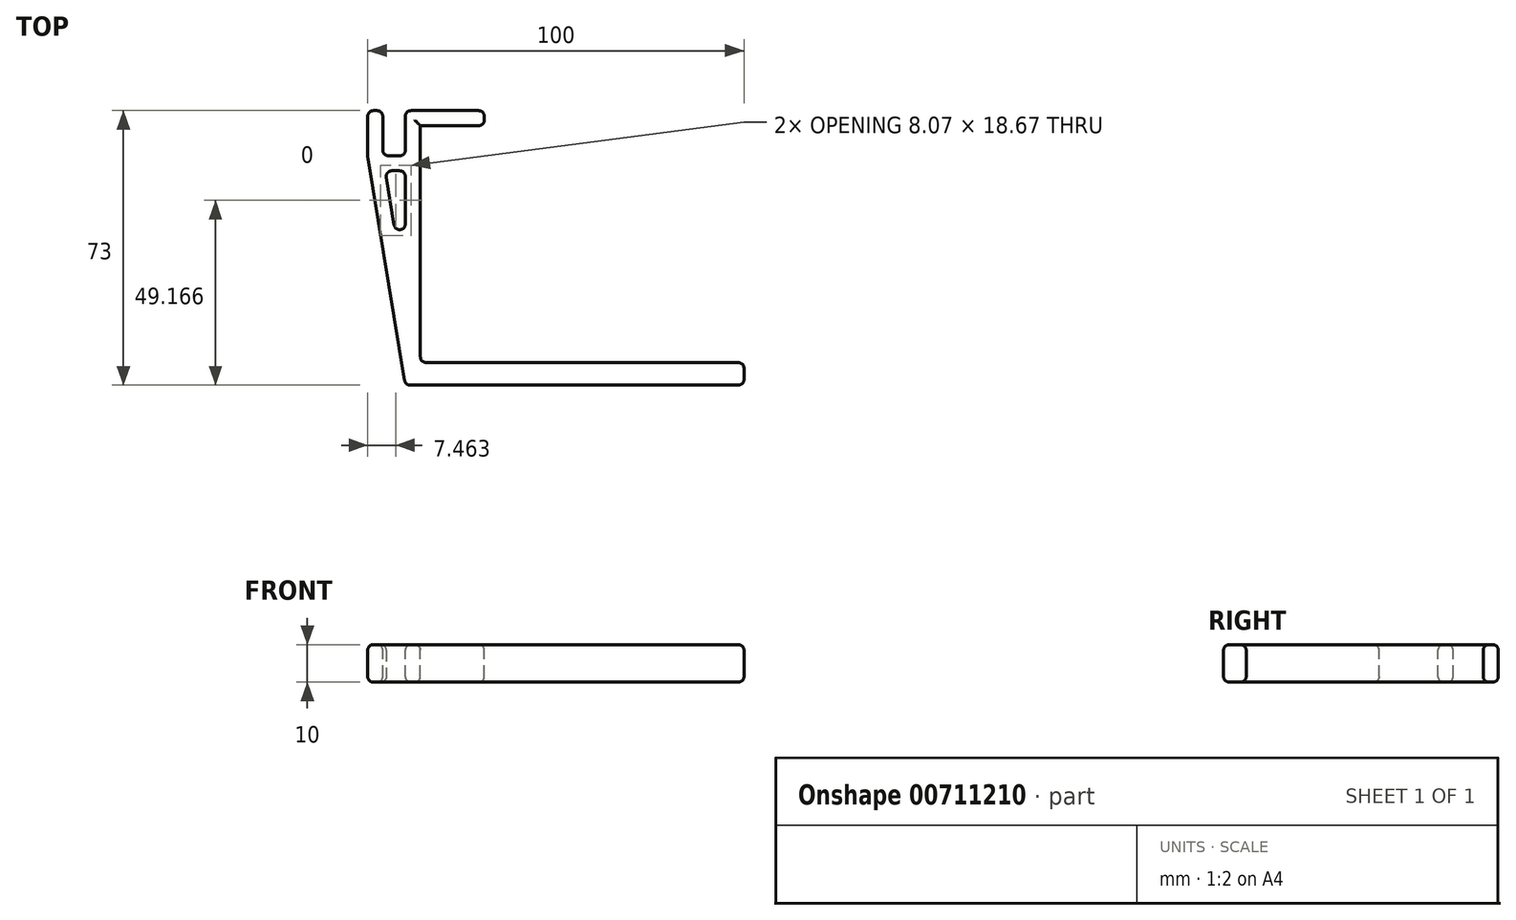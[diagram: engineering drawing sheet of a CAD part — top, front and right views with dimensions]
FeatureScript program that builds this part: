
annotation { "Feature Type Name" : "Feature", "Feature Type Description" : "" }
export const myFeature = defineFeature(function(context is Context, id is Id, definition is map)
    precondition{}
    {
        {
            var Q0;
            Q0=qCreatedBy(makeId("Top.planeOp"),FACE);
            var sketch = newSketch(context, id + "F0", { "sketchPlane" : qUnion([Q0])});
            skLineSegment(sketch, "E0", {"start": v(0, 0) * mm, "end": v(90, 0) * mm});
            skLineSegment(sketch, "E1", {"start": v(90, 6) * mm, "end": v(4, 6) * mm});
            skLineSegment(sketch, "E2", {"start": v(4, 6) * mm, "end": v(4, 69) * mm});
            skLineSegment(sketch, "E3", {"start": v(4, 69) * mm, "end": v(21, 69) * mm});
            skLineSegment(sketch, "E4", {"start": v(21, 69) * mm, "end": v(21, 73) * mm});
            skLineSegment(sketch, "E5", {"start": v(-10, 61) * mm, "end": v(0, 0) * mm});
            skLineSegment(sketch, "E6", {"start": v(21, 73) * mm, "end": v(4, 73) * mm});
            skLineSegment(sketch, "E7", {"start": v(4, 73) * mm, "end": v(0, 73) * mm});
            skLineSegment(sketch, "E8", {"start": v(90, 0) * mm, "end": v(90, 6) * mm});
            skLineSegment(sketch, "E9", {"start": v(0, 61) * mm, "end": v(0, 57) * mm, "construction": true});
            skLineSegment(sketch, "E10", {"start": v(-6, 61) * mm, "end": v(-5.34, 57) * mm, "construction": true});
            skLineSegment(sketch, "E11", {"start": v(0, 57) * mm, "end": v(0, 24.4) * mm});
            skLineSegment(sketch, "E12", {"start": v(0, 24.4) * mm, "end": v(0, 0) * mm, "construction": true});
            skLineSegment(sketch, "E13", {"start": v(-5.34, 57) * mm, "end": v(0, 24.4) * mm});
            skLineSegment(sketch, "E14", {"start": v(4, 57) * mm, "end": v(-9.34, 57) * mm});
            skLineSegment(sketch, "E15", {"start": v(0, 73) * mm, "end": v(0, 69) * mm});
            skLineSegment(sketch, "E16", {"start": v(0, 69) * mm, "end": v(0, 65) * mm});
            skLineSegment(sketch, "E17", {"start": v(0, 65) * mm, "end": v(0, 61) * mm});
            skLineSegment(sketch, "E18", {"start": v(-6, 61) * mm, "end": v(-10, 61) * mm});
            skLineSegment(sketch, "E19", {"start": v(0, 61) * mm, "end": v(-6, 61) * mm});
            skLineSegment(sketch, "E20", {"start": v(-10, 61) * mm, "end": v(-10, 73) * mm});
            skLineSegment(sketch, "E21", {"start": v(-6, 61) * mm, "end": v(-6, 73) * mm});
            skLineSegment(sketch, "E22", {"start": v(-6, 73) * mm, "end": v(-10, 73) * mm});
            skSolve(sketch);
        }
        {
            var Q0;
            Q0=makeQuery(id+"F0.imprint","IMPRINT",FACE,{"disambiguationData":[TD([[makeQuery(id+"F0.imprint","IMPRINT",EDGE,{"derivedFrom":sQuery(id+"F0.wireOp",EDGE,"E18")}),-1.0]])]});
            var Q1;
            {var subQ5=sQuery(id+"F0.wireOp",EDGE,"E3");Q1=makeQuery(id+"F0.imprint","IMPRINT",FACE,{"disambiguationData":[TD([[makeQuery(id+"F0.imprint","IMPRINT",EDGE,{"derivedFrom":subQ5}),1.0]])]});}
            var Q2;
            {var subQ1=sQuery(id+"F0.wireOp",EDGE,"E0");Q2=makeQuery(id+"F0.imprint","IMPRINT",FACE,{"disambiguationData":[TD([[makeQuery(id+"F0.imprint","IMPRINT",EDGE,{"derivedFrom":subQ1}),1.0]])]});}
            extrude(context, id + "F1", {"entities" : qUnion([Q0, Q1, Q2]), "oppositeDirection" : true, "depth" : 10 * mm, "offsetDistance" : 25 * mm});
        }
        {
            var Q0;
            Q0=makeQuery(id+"F1.opExtrude","SWEPT_EDGE",EDGE,{"disambiguationData":[OSD([sQuery(id+"F0.wireOp",EDGE,"E18"),sQuery(id+"F0.wireOp",EDGE,"E19"),sQuery(id+"F0.wireOp",EDGE,"E21")])]});
            var Q1;
            Q1=makeQuery(id+"F1.opExtrude","SWEPT_EDGE",EDGE,{"disambiguationData":[OSD([sQuery(id+"F0.wireOp",EDGE,"E17"),sQuery(id+"F0.wireOp",EDGE,"E19")])]});
            var Q2;
            Q2=makeQuery(id+"F1.opExtrude","SWEPT_EDGE",EDGE,{"disambiguationData":[OSD([sQuery(id+"F0.wireOp",EDGE,"E11"),sQuery(id+"F0.wireOp",EDGE,"E13")])]});
            var Q3;
            Q3=makeQuery(id+"F1.opExtrude","SWEPT_EDGE",EDGE,{"disambiguationData":[OSD([sQuery(id+"F0.wireOp",EDGE,"E1"),sQuery(id+"F0.wireOp",EDGE,"E2")])]});
            var Q4;
            Q4=makeQuery(id+"F1.opExtrude","SWEPT_EDGE",EDGE,{"disambiguationData":[OSD([sQuery(id+"F0.wireOp",EDGE,"E5"),sQuery(id+"F0.wireOp",EDGE,"E18"),sQuery(id+"F0.wireOp",EDGE,"E20")])]});
            var Q5;
            Q5=makeQuery(id+"F1.opExtrude","SWEPT_EDGE",EDGE,{"disambiguationData":[OSD([sQuery(id+"F0.wireOp",EDGE,"E0"),sQuery(id+"F0.wireOp",EDGE,"E5")])]});
            var Q6;
            Q6=makeQuery(id+"F1.opExtrude","SWEPT_EDGE",EDGE,{"disambiguationData":[OSD([sQuery(id+"F0.wireOp",EDGE,"E1"),sQuery(id+"F0.wireOp",EDGE,"E8")])]});
            var Q7;
            Q7=makeQuery(id+"F1.opExtrude","SWEPT_EDGE",EDGE,{"disambiguationData":[OSD([sQuery(id+"F0.wireOp",EDGE,"E0"),sQuery(id+"F0.wireOp",EDGE,"E8")])]});
            var Q8;
            Q8=makeQuery(id+"F1.opExtrude","SWEPT_EDGE",EDGE,{"disambiguationData":[OSD([sQuery(id+"F0.wireOp",EDGE,"E3"),sQuery(id+"F0.wireOp",EDGE,"E4")])]});
            var Q9;
            Q9=makeQuery(id+"F1.opExtrude","SWEPT_EDGE",EDGE,{"disambiguationData":[OSD([sQuery(id+"F0.wireOp",EDGE,"E4"),sQuery(id+"F0.wireOp",EDGE,"E6")])]});
            var Q10;
            Q10=makeQuery(id+"F1.opExtrude","SWEPT_EDGE",EDGE,{"disambiguationData":[OSD([sQuery(id+"F0.wireOp",EDGE,"E7"),sQuery(id+"F0.wireOp",EDGE,"E15")])]});
            var Q11;
            Q11=makeQuery(id+"F1.opExtrude","SWEPT_EDGE",EDGE,{"disambiguationData":[OSD([sQuery(id+"F0.wireOp",EDGE,"E21"),sQuery(id+"F0.wireOp",EDGE,"E22")])]});
            var Q12;
            Q12=makeQuery(id+"F1.opExtrude","SWEPT_EDGE",EDGE,{"disambiguationData":[OSD([sQuery(id+"F0.wireOp",EDGE,"E20"),sQuery(id+"F0.wireOp",EDGE,"E22")])]});
            var Q13;
            Q13=makeQuery(id+"F1.opExtrude","SWEPT_EDGE",EDGE,{"disambiguationData":[OSD([sQuery(id+"F0.wireOp",EDGE,"E11"),sQuery(id+"F0.wireOp",EDGE,"E14")])]});
            var Q14;
            Q14=makeQuery(id+"F1.opExtrude","SWEPT_EDGE",EDGE,{"disambiguationData":[OSD([sQuery(id+"F0.wireOp",EDGE,"E13"),sQuery(id+"F0.wireOp",EDGE,"E14")])]});
            var Q15;
            Q15=makeQuery(id+"F1.opExtrude","CAP_FACE",FACE,{"disambiguationData":[OSD([sQuery(id+"F0.wireOp",EDGE,"E0"),sQuery(id+"F0.wireOp",EDGE,"E1"),sQuery(id+"F0.wireOp",EDGE,"E2"),sQuery(id+"F0.wireOp",EDGE,"E3"),sQuery(id+"F0.wireOp",EDGE,"E4"),sQuery(id+"F0.wireOp",EDGE,"E5"),sQuery(id+"F0.wireOp",EDGE,"E6"),sQuery(id+"F0.wireOp",EDGE,"E7"),sQuery(id+"F0.wireOp",EDGE,"E8"),sQuery(id+"F0.wireOp",EDGE,"E11"),sQuery(id+"F0.wireOp",EDGE,"E13"),sQuery(id+"F0.wireOp",EDGE,"E14"),sQuery(id+"F0.wireOp",EDGE,"E15"),sQuery(id+"F0.wireOp",EDGE,"E16"),sQuery(id+"F0.wireOp",EDGE,"E17"),sQuery(id+"F0.wireOp",EDGE,"E19"),sQuery(id+"F0.wireOp",EDGE,"E20"),sQuery(id+"F0.wireOp",EDGE,"E21"),sQuery(id+"F0.wireOp",EDGE,"E22")])],"isStart":true});
            var Q16;
            Q16=makeQuery(id+"F1.opExtrude","CAP_FACE",FACE,{"disambiguationData":[OSD([sQuery(id+"F0.wireOp",EDGE,"E0"),sQuery(id+"F0.wireOp",EDGE,"E1"),sQuery(id+"F0.wireOp",EDGE,"E2"),sQuery(id+"F0.wireOp",EDGE,"E3"),sQuery(id+"F0.wireOp",EDGE,"E4"),sQuery(id+"F0.wireOp",EDGE,"E5"),sQuery(id+"F0.wireOp",EDGE,"E6"),sQuery(id+"F0.wireOp",EDGE,"E7"),sQuery(id+"F0.wireOp",EDGE,"E8"),sQuery(id+"F0.wireOp",EDGE,"E11"),sQuery(id+"F0.wireOp",EDGE,"E13"),sQuery(id+"F0.wireOp",EDGE,"E14"),sQuery(id+"F0.wireOp",EDGE,"E15"),sQuery(id+"F0.wireOp",EDGE,"E16"),sQuery(id+"F0.wireOp",EDGE,"E17"),sQuery(id+"F0.wireOp",EDGE,"E19"),sQuery(id+"F0.wireOp",EDGE,"E20"),sQuery(id+"F0.wireOp",EDGE,"E21"),sQuery(id+"F0.wireOp",EDGE,"E22")])],"isStart":false});
            fillet(context, id + "F2", {"entities" : qUnion([Q0, Q1, Q2, Q3, Q4, Q5, Q6, Q7, Q8, Q9, Q10, Q11, Q12, Q13, Q14, Q15, Q16]), "radius" : 1.5 * mm, "tangentPropagation" : true, "allowEdgeOverflow" : false});
        }
    });
